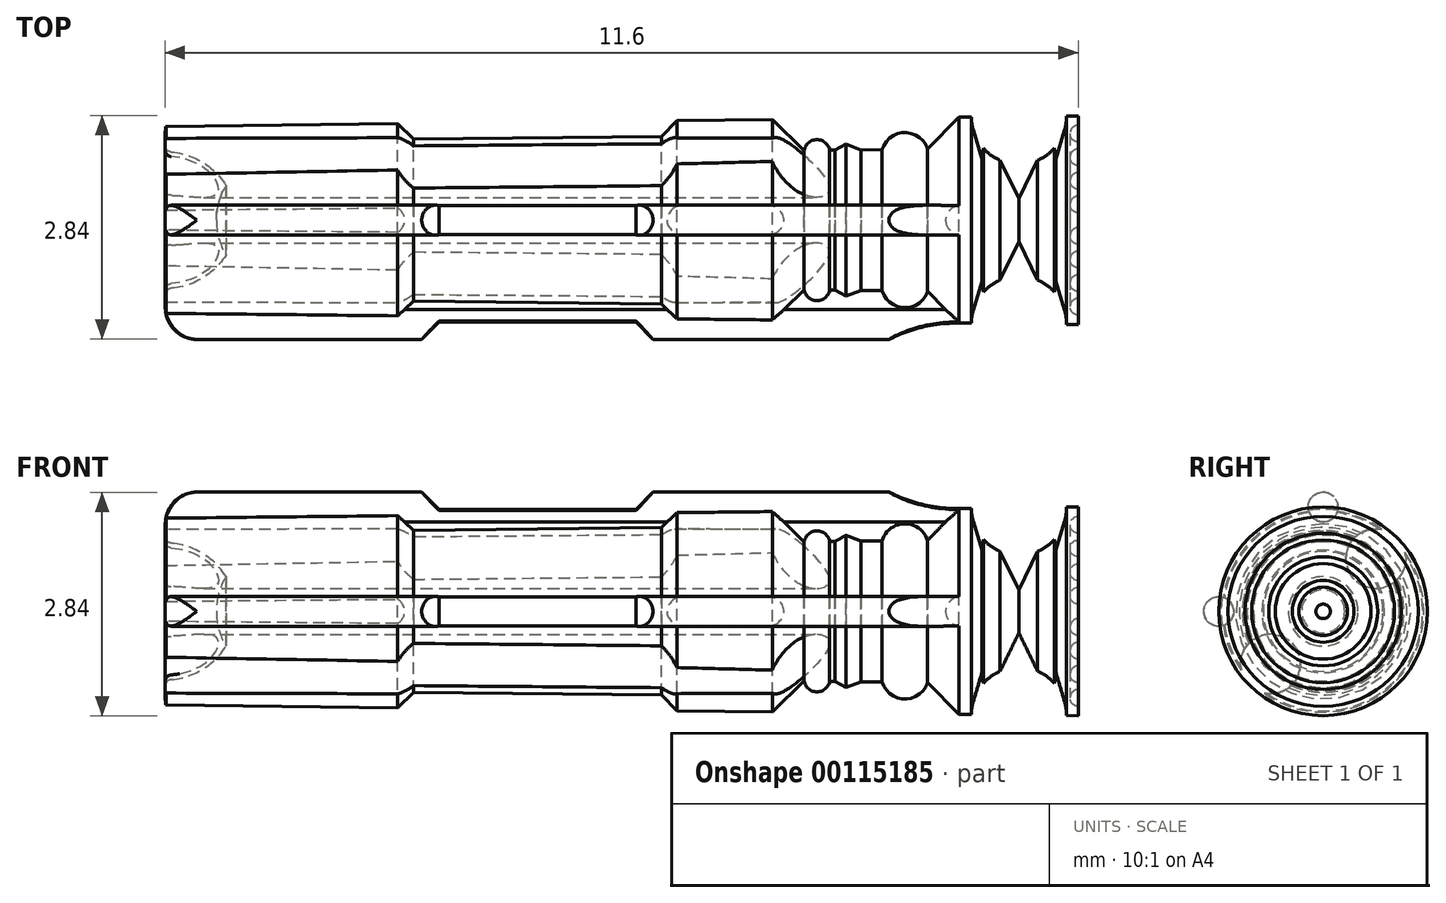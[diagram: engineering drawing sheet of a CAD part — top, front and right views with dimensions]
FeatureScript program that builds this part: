
annotation { "Feature Type Name" : "Feature", "Feature Type Description" : "" }
export const myFeature = defineFeature(function(context is Context, id is Id, definition is map)
    precondition{}
    {
        {
            var Q0;
            Q0=qCreatedBy(makeId("Top.planeOp"),FACE);
            var sketch = newSketch(context, id + "F0", { "sketchPlane" : qUnion([Q0])});
            skLineSegment(sketch, "E0", {"start": v(0, 6) * mm, "end": v(0, -4.69) * mm});
            skLineSegment(sketch, "E1", {"start": v(0, 6) * mm, "end": v(1.33, 6) * mm});
            skLineSegment(sketch, "E2", {"start": v(1.33, 6) * mm, "end": v(1.3, 4.48) * mm});
            skLineSegment(sketch, "E3", {"start": v(1.2, -5.6) * mm, "end": v(0.95, -5.6) * mm});
            skArc(sketch, "E4", {"start": v(0.87, -5.52) * mm, "mid": v(0.74, -5.12) * mm, "end": v(0.44, -4.83) * mm});
            skLineSegment(sketch, "E5", {"start": v(0.87, -5.6) * mm, "end": v(0, -5.6) * mm, "construction": true});
            skLineSegment(sketch, "E6", {"start": v(0, -4.69) * mm, "end": v(0, -4.95) * mm});
            skPoint(sketch, "E7.visualSharp", {"position": v(0.87, -5.6) * mm});
            skArc(sketch, "E7.filletArc", {"start": v(0.87, -5.52) * mm, "mid": v(0.9, -5.58) * mm, "end": v(0.95, -5.6) * mm});
            skLineSegment(sketch, "E8", {"start": v(0, 0) * mm, "end": v(1.26, 0) * mm, "construction": true});
            skArc(sketch, "E9", {"start": v(0, -4.95) * mm, "mid": v(0.23, -4.92) * mm, "end": v(0.44, -4.83) * mm});
            skLineSegment(sketch, "E10", {"start": v(0, -4.95) * mm, "end": v(0, -5.6) * mm, "construction": true});
            skArc(sketch, "E11", {"start": v(0.44, -4.83) * mm, "mid": v(0.23, -4.73) * mm, "end": v(0, -4.69) * mm, "construction": true});
            skArc(sketch, "E12", {"start": v(0.44, -4.83) * mm, "mid": v(0.52, -4.77) * mm, "end": v(0.59, -4.72) * mm, "construction": true});
            skArc(sketch, "E13", {"start": v(0.1, 6) * mm, "mid": v(0.2, 5.9) * mm, "end": v(0.3, 6) * mm});
            skArc(sketch, "E14.1.0.0", {"start": v(0.4, 6) * mm, "mid": v(0.5, 5.9) * mm, "end": v(0.6, 6) * mm});
            skArc(sketch, "E14.2.0.0", {"start": v(0.7, 6) * mm, "mid": v(0.8, 5.9) * mm, "end": v(0.9, 6) * mm});
            skArc(sketch, "E14.3.0.0", {"start": v(1, 6) * mm, "mid": v(1.1, 5.9) * mm, "end": v(1.2, 6) * mm});
            skLineSegment(sketch, "E14.direction1", {"start": v(0.1, 6) * mm, "end": v(0.4, 6) * mm, "construction": true});
            skArc(sketch, "E15.0", {"start": v(1, -5.2) * mm, "mid": v(0.77, -4.84) * mm, "end": v(0.43, -4.6) * mm, "construction": true});
            skLineSegment(sketch, "E15.1", {"start": v(1.12, 5.8) * mm, "end": v(1.1, 4.28) * mm, "construction": true});
            skArc(sketch, "E15.2", {"start": v(0.2, -4.72) * mm, "mid": v(0.32, -4.67) * mm, "end": v(0.43, -4.6) * mm, "construction": true});
            skLineSegment(sketch, "E16.0", {"start": v(0.92, 5.8) * mm, "end": v(0.9, 4.09) * mm, "construction": true});
            skLineSegment(sketch, "E17", {"start": v(1.23, -2.65) * mm, "end": v(1.03, -2.45) * mm});
            skLineSegment(sketch, "E18", {"start": v(1.06, 0.7) * mm, "end": v(1.27, 0.9) * mm});
            skLineSegment(sketch, "E19", {"start": v(1.03, -2.45) * mm, "end": v(1, -5.2) * mm, "construction": true});
            skLineSegment(sketch, "E20", {"start": v(1.06, 0.7) * mm, "end": v(1.03, -2.45) * mm});
            skLineSegment(sketch, "E21", {"start": v(1.23, -2.65) * mm, "end": v(1.2, -5.6) * mm});
            skLineSegment(sketch, "E22", {"start": v(1.27, 0.9) * mm, "end": v(1.23, -2.65) * mm, "construction": true});
            skLineSegment(sketch, "E23", {"start": v(1.28, 2.11) * mm, "end": v(1.08, 2.32) * mm});
            skLineSegment(sketch, "E24", {"start": v(1.3, 4.48) * mm, "end": v(1.1, 4.28) * mm});
            skLineSegment(sketch, "E25", {"start": v(0.88, 2.52) * mm, "end": v(0.8, -5.13) * mm, "construction": true});
            skLineSegment(sketch, "E26", {"start": v(0.9, 4.09) * mm, "end": v(0.9, 3.24) * mm});
            skLineSegment(sketch, "E27", {"start": v(1.08, 2.32) * mm, "end": v(0.88, 2.52) * mm});
            skLineSegment(sketch, "E28", {"start": v(1.1, 4.28) * mm, "end": v(0.9, 4.09) * mm});
            skLineSegment(sketch, "E29", {"start": v(1.08, 2.32) * mm, "end": v(1.06, 0.7) * mm, "construction": true});
            skLineSegment(sketch, "E30", {"start": v(1.1, 4.28) * mm, "end": v(1.08, 2.32) * mm, "construction": true});
            skLineSegment(sketch, "E31", {"start": v(1.28, 2.11) * mm, "end": v(1.27, 0.9) * mm});
            skLineSegment(sketch, "E32", {"start": v(1.3, 4.48) * mm, "end": v(1.28, 2.11) * mm, "construction": true});
            skArc(sketch, "E33", {"start": v(0.88, 2.52) * mm, "mid": v(1.02, 2.68) * mm, "end": v(0.89, 2.84) * mm});
            skArc(sketch, "E34", {"start": v(0.9, 3.5) * mm, "mid": v(1.11, 3.8) * mm, "end": v(0.9, 4.09) * mm});
            skLineSegment(sketch, "E35", {"start": v(0.89, 2.91) * mm, "end": v(0.89, 2.84) * mm});
            skLineSegment(sketch, "E36", {"start": v(0.97, 3.05) * mm, "end": v(0.89, 2.91) * mm});
            skLineSegment(sketch, "E37", {"start": v(0.9, 3.24) * mm, "end": v(0.97, 3.05) * mm});
            skLineSegment(sketch, "E38", {"start": v(0.89, 2.84) * mm, "end": v(0.88, 2.52) * mm});
            skSolve(sketch);
        }
        {
            var Q0;
            {var subQ5=sQuery(id+"F0.wireOp",EDGE,"E0");Q0=makeQuery(id+"F0.imprint","IMPRINT",FACE,{"disambiguationData":[TD([[makeQuery(id+"F0.imprint","IMPRINT",EDGE,{"derivedFrom":subQ5}),1.0]])]});}
            var Q1;
            Q1=makeQuery(id+"F0.imprint","IMPRINT",FACE,{"disambiguationData":[TD([[makeQuery(id+"F0.imprint","IMPRINT",EDGE,{"derivedFrom":sQuery(id+"F0.wireOp",EDGE,"E33")}),1.0]])]});
            var Q2;
            {var subQ0=sQuery(id+"F0.wireOp",EDGE,"E34");Q2=makeQuery(id+"F0.imprint","IMPRINT",FACE,{"disambiguationData":[TD([[makeQuery(id+"F0.imprint","IMPRINT",EDGE,{"derivedFrom":subQ0}),1.0]])]});}
            var Q3;
            Q3=sQuery(id+"F0.wireOp",EDGE,"E0");
            revolve(context, id + "F1", {"entities" : qUnion([Q0, Q1, Q2]), "axis" : qUnion([Q3]), "revolveType" : RevolveType.FULL});
        }
        {
            var Q0;
            Q0=qCreatedBy(makeId("Front.planeOp"),FACE);
            var sketch = newSketch(context, id + "F2", { "sketchPlane" : qUnion([Q0])});
            skLineSegment(sketch, "E39", {"start": v(0, 0) * mm, "end": v(0, 0.95) * mm, "construction": true});
            skLineSegment(sketch, "E40", {"start": v(0, 0) * mm, "end": v(-1.33, 0) * mm, "construction": true});
            skArc(sketch, "E41", {"start": v(-0.95, 0) * mm, "mid": v(-0.87, 0.36) * mm, "end": v(-0.67, 0.67) * mm, "construction": true});
            skArc(sketch, "E42", {"start": v(0, 0.95) * mm, "mid": v(0.67, -0.67) * mm, "end": v(-0.95, 0) * mm, "construction": true});
            skArc(sketch, "E43", {"start": v(0, 1.33) * mm, "mid": v(0.94, -0.94) * mm, "end": v(-1.33, 0) * mm, "construction": true});
            skArc(sketch, "E44", {"start": v(-1.33, 0) * mm, "mid": v(-1.22, 0.5) * mm, "end": v(-0.94, 0.94) * mm, "construction": true});
            skLineSegment(sketch, "E45", {"start": v(0, 0) * mm, "end": v(-0.94, 0.94) * mm, "construction": true});
            skArc(sketch, "E46", {"start": v(-0.94, 0.94) * mm, "mid": v(-0.5, 1.22) * mm, "end": v(0, 1.33) * mm, "construction": true});
            skArc(sketch, "E47", {"start": v(-0.67, 0.67) * mm, "mid": v(-0.36, 0.87) * mm, "end": v(0, 0.95) * mm, "construction": true});
            skCircle(sketch, "E48", {"center": v(-0.67, 0.67) * mm, "radius": 0.38 * mm});
            skCircle(sketch, "E49.MirrorC", {"center": v(0.67, 0.67) * mm, "radius": 0.38 * mm});
            skCircle(sketch, "E50.MirrorC", {"center": v(-0.67, -0.67) * mm, "radius": 0.38 * mm});
            skCircle(sketch, "E51.MirrorC", {"center": v(0.67, -0.67) * mm, "radius": 0.38 * mm});
            skCircle(sketch, "E52", {"center": v(0, 1.33) * mm, "radius": 0.19 * mm});
            skLineSegment(sketch, "E53", {"start": v(0, 0.95) * mm, "end": v(0, 1.33) * mm, "construction": true});
            skPoint(sketch, "E54", {"position": v(0, 1.14) * mm});
            skCircle(sketch, "E55.MirrorC", {"center": v(0, -1.33) * mm, "radius": 0.19 * mm});
            skCircle(sketch, "E56.MirrorC", {"center": v(-1.33, 0) * mm, "radius": 0.19 * mm});
            skCircle(sketch, "E57.MirrorC", {"center": v(1.33, 0) * mm, "radius": 0.19 * mm});
            skSolve(sketch);
        }
        {
            var Q0;
            Q0=makeQuery(id+"F2.imprint","IMPRINT",FACE,{"disambiguationData":[TD([[makeQuery(id+"F2.imprint","IMPRINT",EDGE,{"derivedFrom":sQuery(id+"F2.wireOp",EDGE,"E48")}),1.0]])]});
            var Q1;
            Q1=makeQuery(id+"F2.imprint","IMPRINT",FACE,{"disambiguationData":[TD([[makeQuery(id+"F2.imprint","IMPRINT",EDGE,{"derivedFrom":sQuery(id+"F2.wireOp",EDGE,"E49.MirrorC")}),-1.0]])]});
            var Q2;
            Q2=makeQuery(id+"F2.imprint","IMPRINT",FACE,{"disambiguationData":[TD([[makeQuery(id+"F2.imprint","IMPRINT",EDGE,{"derivedFrom":sQuery(id+"F2.wireOp",EDGE,"E51.MirrorC")}),1.0]])]});
            var Q3;
            Q3=makeQuery(id+"F2.imprint","IMPRINT",FACE,{"disambiguationData":[TD([[makeQuery(id+"F2.imprint","IMPRINT",EDGE,{"derivedFrom":sQuery(id+"F2.wireOp",EDGE,"E50.MirrorC")}),-1.0]])]});
            var Q4;
            Q4=makeQuery(id+"F1.opRevolve","SWEPT_FACE",FACE,{"disambiguationData":[OSD([sQuery(id+"F0.wireOp",EDGE,"E3")])]});
            var Q5;
            Q5=makeQuery(id+"F1.opRevolve","SWEPT_FACE",FACE,{"disambiguationData":[OSD([sQuery(id+"F0.wireOp",EDGE,"E23"),sQuery(id+"F0.wireOp",EDGE,"E27")])]});
            extrude(context, id + "F3", {"entities" : qUnion([Q0, Q1, Q2, Q3]), "operationType" : NewBodyOperationType.REMOVE, "endBound" : BoundingType.UP_TO_SURFACE, "endBoundEntityFace" : qUnion([Q4]), "depth" : 5.84 * mm, "hasSecondDirection" : true, "secondDirectionBound" : BoundingType.UP_TO_SURFACE, "secondDirectionOppositeDirection" : true, "secondDirectionBoundEntityFace" : qUnion([Q5]), "secondDirectionDepth" : 2.4 * mm});
        }
        {
            var Q0;
            Q0=makeQuery(id+"F2.imprint","IMPRINT",FACE,{"disambiguationData":[TD([[makeQuery(id+"F2.imprint","IMPRINT",EDGE,{"derivedFrom":sQuery(id+"F2.wireOp",EDGE,"E56.MirrorC")}),-1.0]])]});
            var Q1;
            Q1=makeQuery(id+"F2.imprint","IMPRINT",FACE,{"disambiguationData":[TD([[makeQuery(id+"F2.imprint","IMPRINT",EDGE,{"derivedFrom":sQuery(id+"F2.wireOp",EDGE,"E55.MirrorC")}),-1.0]])]});
            var Q2;
            Q2=makeQuery(id+"F2.imprint","IMPRINT",FACE,{"disambiguationData":[TD([[makeQuery(id+"F2.imprint","IMPRINT",EDGE,{"derivedFrom":sQuery(id+"F2.wireOp",EDGE,"E57.MirrorC")}),1.0]])]});
            var Q3;
            Q3=makeQuery(id+"F2.imprint","IMPRINT",FACE,{"disambiguationData":[TD([[makeQuery(id+"F2.imprint","IMPRINT",EDGE,{"derivedFrom":sQuery(id+"F2.wireOp",EDGE,"E52")}),1.0]])]});
            var Q4;
            Q4=makeQuery(id+"F3.boolean.opBoolean","SPLIT",FACE,{"disambiguationData":[TD([makeQuery(id+"F1.opRevolve","SWEPT_FACE",FACE,{"disambiguationData":[OSD([sQuery(id+"F0.wireOp",EDGE,"E7.filletArc")])]}),makeQuery(id+"F1.opRevolve","SWEPT_FACE",FACE,{"disambiguationData":[OSD([sQuery(id+"F0.wireOp",EDGE,"E21")])]}),makeQuery(id+"F3.opExtrude","SWEPT_FACE",FACE,{"disambiguationData":[OSD([sQuery(id+"F2.wireOp",EDGE,"E48")])]}),makeQuery(id+"F3.opExtrude","SWEPT_FACE",FACE,{"disambiguationData":[OSD([sQuery(id+"F2.wireOp",EDGE,"E49.MirrorC")])]})])],"derivedFrom":makeQuery(id+"F1.opRevolve","SWEPT_FACE",FACE,{"disambiguationData":[OSD([sQuery(id+"F0.wireOp",EDGE,"E3")])]})});
            var Q5;
            Q5=makeQuery(id+"F1.opRevolve","SWEPT_FACE",FACE,{"disambiguationData":[OSD([sQuery(id+"F0.wireOp",EDGE,"E24"),sQuery(id+"F0.wireOp",EDGE,"E28")])]});
            extrude(context, id + "F4", {"entities" : qUnion([Q0, Q1, Q2, Q3]), "operationType" : NewBodyOperationType.ADD, "endBound" : BoundingType.UP_TO_SURFACE, "endBoundEntityFace" : qUnion([Q4]), "depth" : 25 * mm, "hasSecondDirection" : true, "secondDirectionBound" : BoundingType.UP_TO_SURFACE, "secondDirectionOppositeDirection" : true, "secondDirectionBoundEntityFace" : qUnion([Q5]), "secondDirectionDepth" : 25 * mm});
        }
        {
            var Q0;
            Q0=qCreatedBy(makeId("Top.planeOp"),FACE);
            var sketch = newSketch(context, id + "F5", { "sketchPlane" : qUnion([Q0])});
            skLineSegment(sketch, "E58.0", {"start": v(-1.33, 6) * mm, "end": v(1.33, 6) * mm});
            skLineSegment(sketch, "E59", {"start": v(1.33, 6) * mm, "end": v(1.32, 5.85) * mm});
            skLineSegment(sketch, "E60", {"start": v(1.51, 4.68) * mm, "end": v(1.51, 3.6) * mm, "construction": true});
            skLineSegment(sketch, "E61", {"start": v(0, 0) * mm, "end": v(0, 6) * mm});
            skLineSegment(sketch, "E62", {"start": v(0, 0) * mm, "end": v(0, -5.6) * mm});
            skLineSegment(sketch, "E63.0", {"start": v(0, -5.6) * mm, "end": v(1.11, -5.6) * mm});
            skPoint(sketch, "E64.orphan", {"position": v(0.13, -5.6) * mm});
            skPoint(sketch, "E65.orphan", {"position": v(0.58, -5.6) * mm});
            skPoint(sketch, "E66.visualSharp", {"position": v(1.51, -5.6) * mm});
            skArc(sketch, "E66.filletArc", {"start": v(1.11, -5.6) * mm, "mid": v(1.4, -5.48) * mm, "end": v(1.51, -5.2) * mm});
            skLineSegment(sketch, "E67", {"start": v(1.51, -2.34) * mm, "end": v(1.51, -5.2) * mm});
            skLineSegment(sketch, "E68", {"start": v(1.51, 0.6) * mm, "end": v(1.51, -2.34) * mm, "construction": true});
            skLineSegment(sketch, "E69", {"start": v(1.51, -2.34) * mm, "end": v(1.3, -2.12) * mm});
            skLineSegment(sketch, "E70", {"start": v(1.3, -2.12) * mm, "end": v(1.3, 0.38) * mm});
            skLineSegment(sketch, "E71", {"start": v(1.3, 0.38) * mm, "end": v(1.51, 0.6) * mm});
            skArc(sketch, "E72", {"start": v(1.3, 4.49) * mm, "mid": v(1.36, 4.03) * mm, "end": v(1.51, 3.6) * mm});
            skLineSegment(sketch, "E73", {"start": v(1.51, 3.6) * mm, "end": v(1.51, 0.6) * mm});
            skArc(sketch, "E74", {"start": v(1.32, 5.85) * mm, "mid": v(0.71, 5.25) * mm, "end": v(1.3, 4.64) * mm});
            skLineSegment(sketch, "E75", {"start": v(1.3, 4.64) * mm, "end": v(1.3, 4.49) * mm});
            skLineSegment(sketch, "E76", {"start": v(1.32, 5.85) * mm, "end": v(1.3, 4.64) * mm, "construction": true});
            skLineSegment(sketch, "E77", {"start": v(1.14, 4.67) * mm, "end": v(1.14, 5.82) * mm, "construction": true});
            skLineSegment(sketch, "E78", {"start": v(1.14, 4.67) * mm, "end": v(0.78, 4.78) * mm});
            skLineSegment(sketch, "E79", {"start": v(0.78, 4.78) * mm, "end": v(1.14, 4.82) * mm});
            skLineSegment(sketch, "E80", {"start": v(1.14, 4.82) * mm, "end": v(0.78, 5) * mm});
            skLineSegment(sketch, "E81", {"start": v(0.27, 5.25) * mm, "end": v(1.14, 5.67) * mm});
            skLineSegment(sketch, "E82", {"start": v(1.14, 5.67) * mm, "end": v(0.78, 5.71) * mm});
            skLineSegment(sketch, "E83", {"start": v(0.78, 5.71) * mm, "end": v(1.14, 5.82) * mm});
            skLineSegment(sketch, "E84", {"start": v(0.27, 5.25) * mm, "end": v(1.32, 5.25) * mm, "construction": true});
            skLineSegment(sketch, "E85", {"start": v(0.78, 4.78) * mm, "end": v(0.78, 5) * mm, "construction": true});
            skLineSegment(sketch, "E86", {"start": v(0.78, 5.25) * mm, "end": v(0.78, 5.5) * mm, "construction": true});
            skLineSegment(sketch, "E87", {"start": v(0.78, 5) * mm, "end": v(0.27, 5.25) * mm});
            skLineSegment(sketch, "E88", {"start": v(0.78, 5.5) * mm, "end": v(0.78, 5.71) * mm, "construction": true});
            skLineSegment(sketch, "E89", {"start": v(0.78, 5) * mm, "end": v(0.78, 5.25) * mm, "construction": true});
            skSolve(sketch);
        }
        {
            var Q0;
            {var subQ14=sQuery(id+"F5.wireOp",EDGE,"E59");Q0=makeQuery(id+"F5.imprint","IMPRINT",FACE,{"disambiguationData":[TD([[makeQuery(id+"F5.imprint","IMPRINT",EDGE,{"derivedFrom":subQ14}),-1.0]])]});}
            var Q1;
            Q1=sQuery(id+"F5.wireOp",EDGE,"E61");
            revolve(context, id + "F6", {"operationType" : NewBodyOperationType.INTERSECT, "entities" : qUnion([Q0]), "axis" : qUnion([Q1]), "revolveType" : RevolveType.FULL});
        }
        {
            var Q0;
            Q0=makeQuery(id+"F1.opRevolve","SWEPT_BODY",BODY,{"disambiguationData":[OSD([sQuery(id+"F0.wireOp",EDGE,"E0"),sQuery(id+"F0.wireOp",EDGE,"E1"),sQuery(id+"F0.wireOp",EDGE,"E2"),sQuery(id+"F0.wireOp",EDGE,"E3"),sQuery(id+"F0.wireOp",EDGE,"E4"),sQuery(id+"F0.wireOp",EDGE,"E6"),sQuery(id+"F0.wireOp",EDGE,"E7.filletArc"),sQuery(id+"F0.wireOp",EDGE,"E9"),sQuery(id+"F0.wireOp",EDGE,"E13"),sQuery(id+"F0.wireOp",EDGE,"E14.1.0.0"),sQuery(id+"F0.wireOp",EDGE,"E14.2.0.0"),sQuery(id+"F0.wireOp",EDGE,"E14.3.0.0"),sQuery(id+"F0.wireOp",EDGE,"E17"),sQuery(id+"F0.wireOp",EDGE,"E18"),sQuery(id+"F0.wireOp",EDGE,"E20"),sQuery(id+"F0.wireOp",EDGE,"E21"),sQuery(id+"F0.wireOp",EDGE,"E23"),sQuery(id+"F0.wireOp",EDGE,"E24"),sQuery(id+"F0.wireOp",EDGE,"E26"),sQuery(id+"F0.wireOp",EDGE,"E27"),sQuery(id+"F0.wireOp",EDGE,"E28"),sQuery(id+"F0.wireOp",EDGE,"E31"),sQuery(id+"F0.wireOp",EDGE,"E33"),sQuery(id+"F0.wireOp",EDGE,"E34"),sQuery(id+"F0.wireOp",EDGE,"E35"),sQuery(id+"F0.wireOp",EDGE,"E36"),sQuery(id+"F0.wireOp",EDGE,"E37")])]});
            var Q1;
            Q1=sQuery(id+"F2.wireOp",EDGE,"E39");
            transform(context, id + "F7", {"entities" : qUnion([Q0]), "transformType" : TransformType.ROTATION, "transformAxis" : qUnion([Q1]), "angle" : 90 * degree, "oppositeDirection" : true, "makeCopy" : false});
        }
    });
